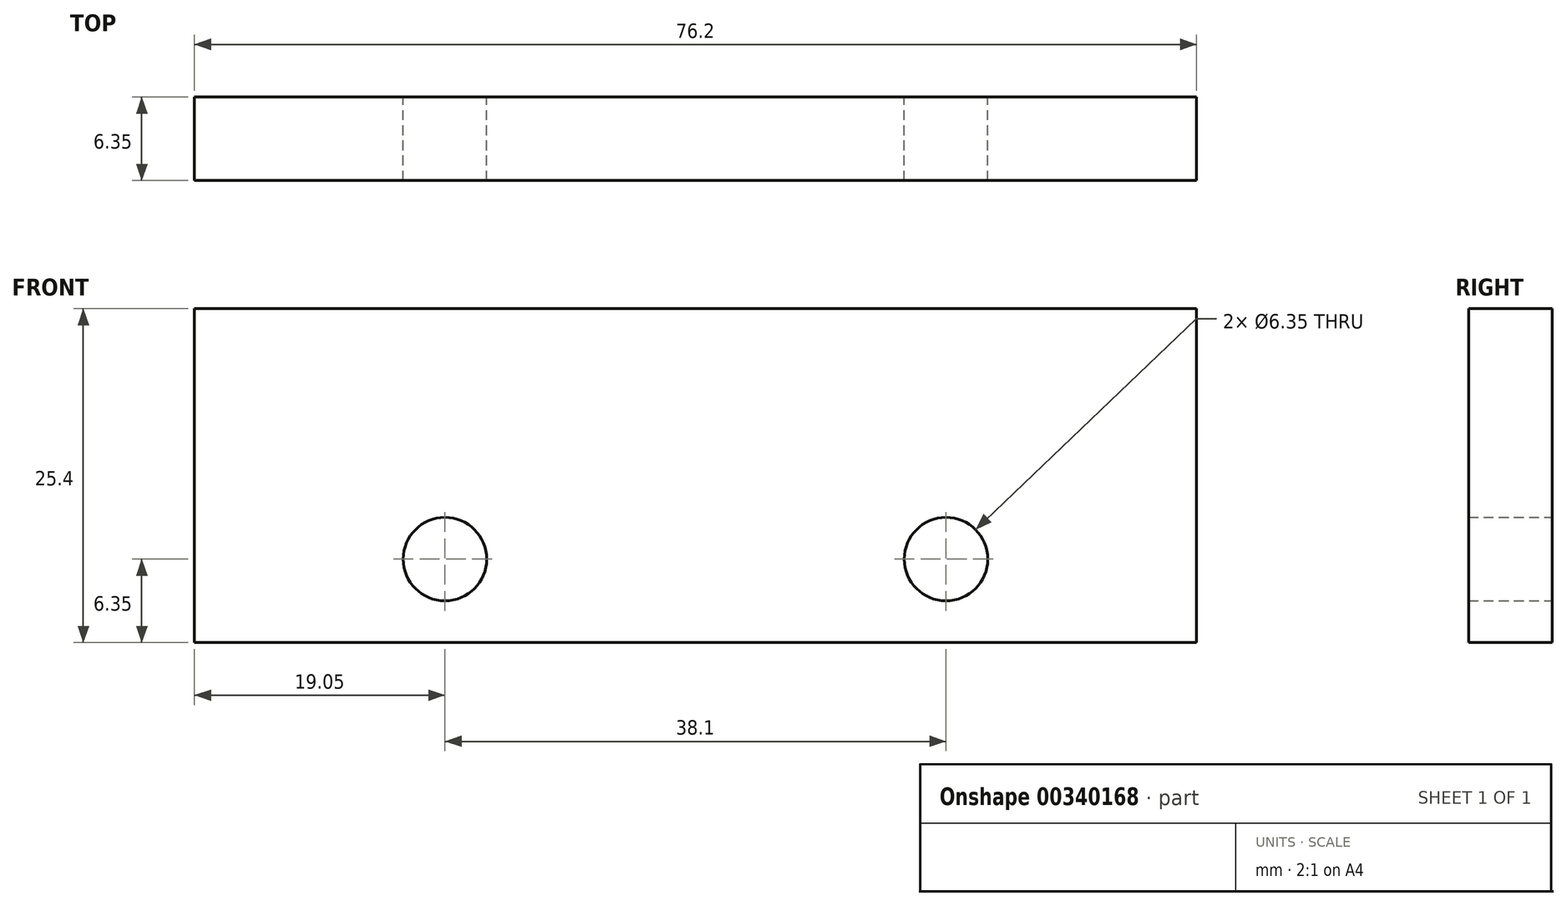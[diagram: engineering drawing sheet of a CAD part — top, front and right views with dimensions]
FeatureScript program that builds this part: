
annotation { "Feature Type Name" : "Feature", "Feature Type Description" : "" }
export const myFeature = defineFeature(function(context is Context, id is Id, definition is map)
    precondition{}
    {
        {
            var Q0;
            Q0=qCreatedBy(makeId("Front.planeOp"),FACE);
            var sketch = newSketch(context, id + "F0", { "sketchPlane" : qUnion([Q0])});
            skLineSegment(sketch, "E0.bottom", {"start": v(0, 0) * mm, "end": v(76.2, 0) * mm});
            skLineSegment(sketch, "E0.top", {"start": v(0, 25.4) * mm, "end": v(76.2, 25.4) * mm});
            skLineSegment(sketch, "E0.left", {"start": v(0, 0) * mm, "end": v(0, 25.4) * mm});
            skLineSegment(sketch, "E0.right", {"start": v(76.2, 0) * mm, "end": v(76.2, 25.4) * mm});
            skCircle(sketch, "E1", {"center": v(19.05, 6.35) * mm, "radius": 3.18 * mm});
            skCircle(sketch, "E2", {"center": v(57.15, 6.35) * mm, "radius": 3.18 * mm});
            skSolve(sketch);
        }
        {
            var Q0;
            Q0 = qSketchRegion(id + "F0", true);
            extrude(context, id + "F1", {"entities" : qUnion([Q0]), "depth" : 6.35 * mm});
        }
    });
